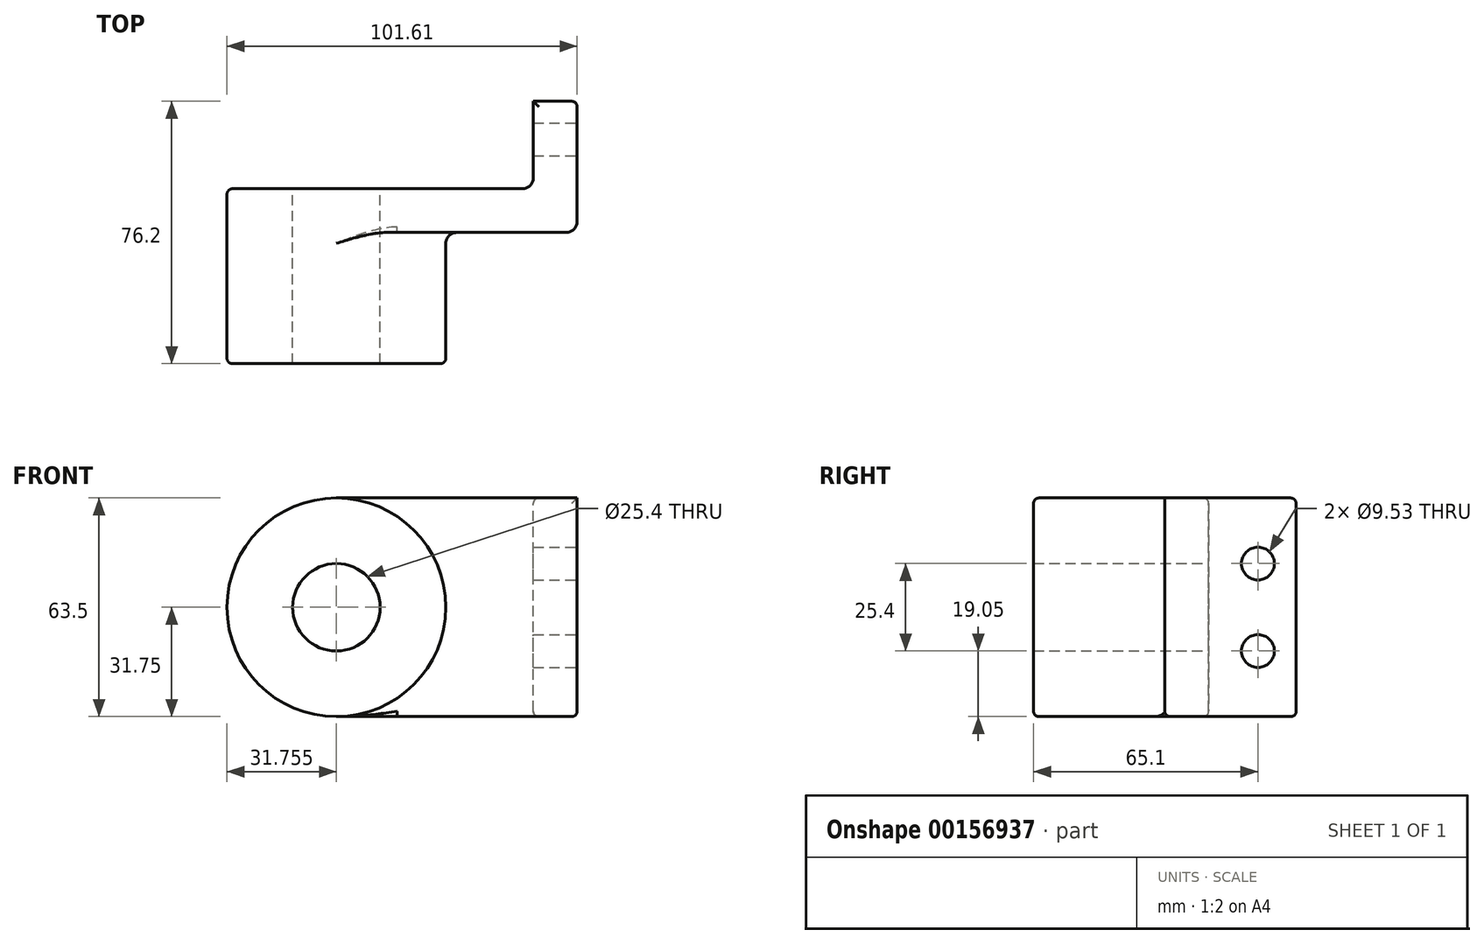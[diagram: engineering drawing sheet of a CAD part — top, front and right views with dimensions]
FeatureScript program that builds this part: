
annotation { "Feature Type Name" : "Feature", "Feature Type Description" : "" }
export const myFeature = defineFeature(function(context is Context, id is Id, definition is map)
    precondition{}
    {
        {
            var Q0;
            Q0=qCreatedBy(makeId("Front.planeOp"),FACE);
            var sketch = newSketch(context, id + "F0", { "sketchPlane" : qUnion([Q0])});
            skLineSegment(sketch, "E0.bottom", {"start": v(-34.92, -31.75) * mm, "end": v(34.93, -31.75) * mm});
            skLineSegment(sketch, "E0.top", {"start": v(-34.92, 31.75) * mm, "end": v(34.93, 31.75) * mm});
            skLineSegment(sketch, "E0.left", {"start": v(-34.92, -31.75) * mm, "end": v(-34.92, 31.75) * mm});
            skLineSegment(sketch, "E0.right", {"start": v(34.93, -31.75) * mm, "end": v(34.93, 31.75) * mm});
            skPoint(sketch, "E0.middle", {"position": v(0, 0) * mm});
            skCircle(sketch, "E1", {"center": v(-34.92, 0) * mm, "radius": 31.75 * mm});
            skCircle(sketch, "E2", {"center": v(-34.92, 0) * mm, "radius": 12.7 * mm});
            skSolve(sketch);
        }
        {
            var Q0;
            {var subQ1=sQuery(id+"F0.wireOp",EDGE,"E0.left");var subQ3=sQuery(id+"F0.wireOp",EDGE,"E2");var subQ4=makeQuery(id+"F0.imprint","INTERSECT",VERTEX,{"disambiguationData":[OD(0.0)],"derivedFrom":[subQ1,subQ3]});Q0=makeQuery(id+"F0.imprint","IMPRINT",FACE,{"disambiguationData":[TD([[makeQuery(id+"F0.imprint","IMPRINT",EDGE,{"disambiguationData":[TD([[subQ4,-1.0]])],"derivedFrom":subQ3}),-1.0]])]});}
            var Q1;
            {var subQ0=sQuery(id+"F0.wireOp",EDGE,"E2");var subQ1=sQuery(id+"F0.wireOp",EDGE,"E0.left");var subQ2=makeQuery(id+"F0.imprint","INTERSECT",VERTEX,{"disambiguationData":[OD(0.0)],"derivedFrom":[subQ1,subQ0]});Q1=makeQuery(id+"F0.imprint","IMPRINT",FACE,{"disambiguationData":[TD([[makeQuery(id+"F0.imprint","IMPRINT",EDGE,{"disambiguationData":[TD([[subQ2,-1.0]])],"derivedFrom":subQ1}),-1.0]])]});}
            var Q2;
            {var subQ0=sQuery(id+"F0.wireOp",EDGE,"E2");var subQ1=sQuery(id+"F0.wireOp",EDGE,"E0.left");var subQ2=makeQuery(id+"F0.imprint","INTERSECT",VERTEX,{"disambiguationData":[OD(0.0)],"derivedFrom":[subQ1,subQ0]});Q2=makeQuery(id+"F0.imprint","IMPRINT",FACE,{"disambiguationData":[TD([[makeQuery(id+"F0.imprint","IMPRINT",EDGE,{"disambiguationData":[TD([[subQ2,-1.0]])],"derivedFrom":subQ1}),1.0]])]});}
            var Q3;
            {var subQ1=sQuery(id+"F0.wireOp",EDGE,"E0.left");var subQ3=sQuery(id+"F0.wireOp",EDGE,"E2");var subQ4=makeQuery(id+"F0.imprint","INTERSECT",VERTEX,{"disambiguationData":[OD(0.0)],"derivedFrom":[subQ1,subQ3]});Q3=makeQuery(id+"F0.imprint","IMPRINT",FACE,{"disambiguationData":[TD([[makeQuery(id+"F0.imprint","IMPRINT",EDGE,{"disambiguationData":[TD([[subQ4,1.0]])],"derivedFrom":subQ3}),-1.0]])]});}
            var Q4;
            {var subQ0=sQuery(id+"F0.wireOp",EDGE,"E0.bottom");Q4=makeQuery(id+"F0.imprint","IMPRINT",FACE,{"disambiguationData":[TD([[makeQuery(id+"F0.imprint","IMPRINT",EDGE,{"derivedFrom":subQ0}),1.0]])]});}
            extrude(context, id + "F1", {"entities" : qUnion([Q0, Q1, Q2, Q3, Q4]), "depth" : 12.7 * mm});
        }
        {
            var Q0;
            {var subQ1=sQuery(id+"F0.wireOp",EDGE,"E0.left");var subQ3=sQuery(id+"F0.wireOp",EDGE,"E2");var subQ4=makeQuery(id+"F0.imprint","INTERSECT",VERTEX,{"disambiguationData":[OD(0.0)],"derivedFrom":[subQ1,subQ3]});Q0=makeQuery(id+"F0.imprint","IMPRINT",FACE,{"disambiguationData":[TD([[makeQuery(id+"F0.imprint","IMPRINT",EDGE,{"disambiguationData":[TD([[subQ4,1.0]])],"derivedFrom":subQ3}),-1.0]])]});}
            var Q1;
            {var subQ1=sQuery(id+"F0.wireOp",EDGE,"E0.left");var subQ3=sQuery(id+"F0.wireOp",EDGE,"E2");var subQ4=makeQuery(id+"F0.imprint","INTERSECT",VERTEX,{"disambiguationData":[OD(0.0)],"derivedFrom":[subQ1,subQ3]});Q1=makeQuery(id+"F0.imprint","IMPRINT",FACE,{"disambiguationData":[TD([[makeQuery(id+"F0.imprint","IMPRINT",EDGE,{"disambiguationData":[TD([[subQ4,-1.0]])],"derivedFrom":subQ3}),-1.0]])]});}
            extrude(context, id + "F2", {"entities" : qUnion([Q0, Q1]), "operationType" : NewBodyOperationType.ADD, "depth" : 50.8 * mm});
        }
        {
            var Q0;
            Q0=makeQuery(id+"F1.opExtrude","SWEPT_FACE",FACE,{"disambiguationData":[OSD([sQuery(id+"F0.wireOp",EDGE,"E0.right")])]});
            var sketch = newSketch(context, id + "F3", { "sketchPlane" : qUnion([Q0])});
            skLineSegment(sketch, "E3.bottom", {"start": v(-12.7, -31.75) * mm, "end": v(25.4, -31.75) * mm});
            skLineSegment(sketch, "E3.top", {"start": v(-12.7, 31.75) * mm, "end": v(25.4, 31.75) * mm});
            skLineSegment(sketch, "E3.left", {"start": v(-12.7, -31.75) * mm, "end": v(-12.7, 31.75) * mm});
            skLineSegment(sketch, "E3.right", {"start": v(25.4, -31.75) * mm, "end": v(25.4, 31.75) * mm});
            skCircle(sketch, "E4", {"center": v(14.3, -12.7) * mm, "radius": 4.76 * mm});
            skLineSegment(sketch, "E5", {"start": v(-12.7, 0) * mm, "end": v(25.4, 0) * mm, "construction": true});
            skCircle(sketch, "E6.MirrorC", {"center": v(14.3, 12.7) * mm, "radius": 4.76 * mm});
            skSolve(sketch);
        }
        {
            var Q0;
            Q0 = qSketchRegion(id + "F3", true);
            extrude(context, id + "F4", {"entities" : qUnion([Q0]), "operationType" : NewBodyOperationType.ADD, "oppositeDirection" : true, "depth" : 12.7 * mm});
        }
        {
            var Q0;
            {var subQ0=sQuery(id+"F0.wireOp",EDGE,"E1");Q0=makeQuery(id+"F2.boolean.opBoolean","INTERSECT",EDGE,{"derivedFrom":[makeQuery(id+"F1.opExtrude","CAP_FACE",FACE,{"disambiguationData":[OSD([sQuery(id+"F0.wireOp",EDGE,"E0.bottom"),sQuery(id+"F0.wireOp",EDGE,"E0.top"),sQuery(id+"F0.wireOp",EDGE,"E0.right"),subQ0])],"isStart":false}),makeQuery(id+"F2.opExtrude","SWEPT_FACE",FACE,{"disambiguationData":[OSD([subQ0])]})]});}
            var Q1;
            Q1=makeQuery(id+"F1.opExtrude","CAP_EDGE",EDGE,{"disambiguationData":[OSD([sQuery(id+"F0.wireOp",EDGE,"E0.right")])],"isStart":false});
            var Q2;
            Q2=makeQuery(id+"F4.boolean.opBoolean","INTERSECT",EDGE,{"derivedFrom":[makeQuery(id+"F1.opExtrude","CAP_FACE",FACE,{"disambiguationData":[OSD([sQuery(id+"F0.wireOp",EDGE,"E0.bottom"),sQuery(id+"F0.wireOp",EDGE,"E0.top"),sQuery(id+"F0.wireOp",EDGE,"E0.right"),sQuery(id+"F0.wireOp",EDGE,"E1")])],"isStart":true}),makeQuery(id+"F4.opExtrude","CAP_FACE",FACE,{"disambiguationData":[OSD([sQuery(id+"F3.wireOp",EDGE,"E3.bottom"),sQuery(id+"F3.wireOp",EDGE,"E3.top"),sQuery(id+"F3.wireOp",EDGE,"E3.left"),sQuery(id+"F3.wireOp",EDGE,"E3.right"),sQuery(id+"F3.wireOp",EDGE,"E4"),sQuery(id+"F3.wireOp",EDGE,"E6.MirrorC")])],"isStart":false})]});
            fillet(context, id + "F5", {"entities" : qUnion([Q0, Q1, Q2]), "radius" : 3.17 * mm, "tangentPropagation" : true, "allowEdgeOverflow" : false});
        }
        {
            var Q0;
            Q0=makeQuery(id+"F2.opExtrude","CAP_EDGE",EDGE,{"disambiguationData":[OSD([sQuery(id+"F0.wireOp",EDGE,"E1")])],"isStart":false});
            var Q1;
            Q1=makeQuery(id+"F1.opExtrude","CAP_EDGE",EDGE,{"disambiguationData":[OSD([sQuery(id+"F0.wireOp",EDGE,"E0.bottom")])],"isStart":false});
            var Q2;
            Q2=makeQuery(id+"F1.opExtrude","CAP_EDGE",EDGE,{"disambiguationData":[OSD([sQuery(id+"F0.wireOp",EDGE,"E0.bottom")])],"isStart":true});
            var Q3;
            Q3=makeQuery(id+"F4.opExtrude","CAP_EDGE",EDGE,{"disambiguationData":[OSD([sQuery(id+"F3.wireOp",EDGE,"E3.right")])],"isStart":true});
            var Q4;
            Q4=makeQuery(id+"F4.opExtrude","SWEPT_EDGE",EDGE,{"disambiguationData":[OSD([sQuery(id+"F3.wireOp",EDGE,"E3.bottom"),sQuery(id+"F3.wireOp",EDGE,"E3.right")])]});
            var Q5;
            Q5=makeQuery(id+"F4.opExtrude","SWEPT_EDGE",EDGE,{"disambiguationData":[OSD([sQuery(id+"F3.wireOp",EDGE,"E3.top"),sQuery(id+"F3.wireOp",EDGE,"E3.right")])]});
            fillet(context, id + "F6", {"entities" : qUnion([Q0, Q1, Q2, Q3, Q4, Q5]), "radius" : 1.57 * mm, "tangentPropagation" : true, "allowEdgeOverflow" : false});
        }
    });
